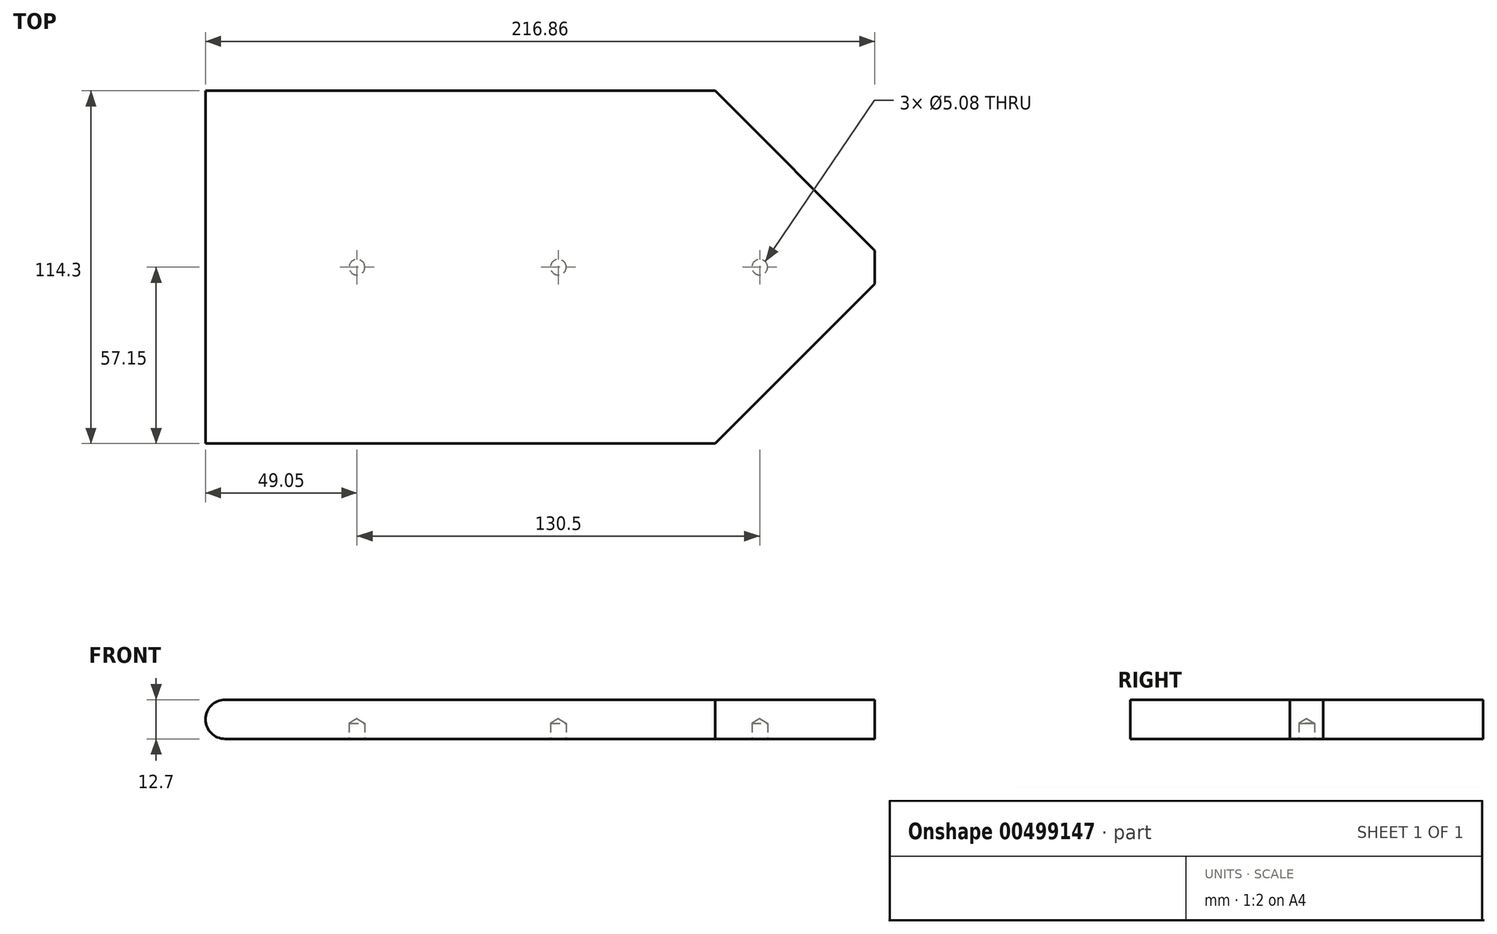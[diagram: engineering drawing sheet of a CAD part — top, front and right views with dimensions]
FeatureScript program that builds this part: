
annotation { "Feature Type Name" : "Feature", "Feature Type Description" : "" }
export const myFeature = defineFeature(function(context is Context, id is Id, definition is map)
    precondition{}
    {
        {
            var Q0;
            Q0=qCreatedBy(makeId("Top.planeOp"),FACE);
            var sketch = newSketch(context, id + "F0", { "sketchPlane" : qUnion([Q0])});
            skLineSegment(sketch, "E0.bottom", {"start": v(114.3, 57.15) * mm, "end": v(82.55, 57.15) * mm});
            skLineSegment(sketch, "E0.top", {"start": v(114.3, -57.15) * mm, "end": v(82.55, -57.15) * mm});
            skLineSegment(sketch, "E0.left", {"start": v(114.3, 57.15) * mm, "end": v(114.3, 27.94) * mm});
            skLineSegment(sketch, "E0.right", {"start": v(-114.3, 57.15) * mm, "end": v(-114.3, -57.15) * mm});
            skPoint(sketch, "E0.middle", {"position": v(0, 0) * mm});
            skLineSegment(sketch, "E1", {"start": v(0, 0) * mm, "end": v(65.25, 0) * mm});
            skLineSegment(sketch, "E2", {"start": v(65.25, 0) * mm, "end": v(0, 0) * mm, "construction": true});
            skLineSegment(sketch, "E3", {"start": v(-65.25, 0) * mm, "end": v(0, 0) * mm, "construction": true});
            skPoint(sketch, "E4", {"position": v(-65.25, 0) * mm});
            skPoint(sketch, "E5", {"position": v(65.25, 0) * mm});
            skPoint(sketch, "E6", {"position": v(126.87, 10.64) * mm});
            skLineSegment(sketch, "E7", {"start": v(82.55, -57.15) * mm, "end": v(82.55, -27.94) * mm, "construction": true});
            skLineSegment(sketch, "E8", {"start": v(82.55, -27.94) * mm, "end": v(114.3, -27.94) * mm, "construction": true});
            skLineSegment(sketch, "E9", {"start": v(82.55, 27.94) * mm, "end": v(114.3, 27.94) * mm, "construction": true});
            skLineSegment(sketch, "E10", {"start": v(82.55, 27.94) * mm, "end": v(82.55, 57.15) * mm, "construction": true});
            skLineSegment(sketch, "E11", {"start": v(114.3, -27.94) * mm, "end": v(114.3, -57.15) * mm});
            skLineSegment(sketch, "E12", {"start": v(114.3, 27.94) * mm, "end": v(114.3, -27.94) * mm});
            skLineSegment(sketch, "E13", {"start": v(82.55, -57.15) * mm, "end": v(-114.3, -57.15) * mm});
            skLineSegment(sketch, "E14", {"start": v(82.55, 57.15) * mm, "end": v(-114.3, 57.15) * mm});
            skSolve(sketch);
        }
        {
            var Q0;
            Q0=makeQuery(id+"F0.imprint","IMPRINT",FACE,{"disambiguationData":[TD([[makeQuery(id+"F0.imprint","IMPRINT",EDGE,{"derivedFrom":sQuery(id+"F0.wireOp",EDGE,"E0.right")}),1.0]])]});
            extrude(context, id + "F1", {"entities" : qUnion([Q0]), "depth" : 12.7 * mm});
        }
        {
            var Q0;
            Q0=sQuery(id+"F0.wireOp",VERTEX,"E4");
            var Q1;
            Q1=makeQuery(id+"F1.opExtrude","SWEPT_BODY",BODY,{"disambiguationData":[OSD([sQuery(id+"F0.wireOp",EDGE,"E0.bottom"),sQuery(id+"F0.wireOp",EDGE,"E0.top"),sQuery(id+"F0.wireOp",EDGE,"E0.left"),sQuery(id+"F0.wireOp",EDGE,"E0.right")])]});
            hole(context, id + "F2", {"style" : HoleStyle.SIMPLE, "endStyle" : HoleEndStyle.BLIND, "oppositeDirection" : true, "holeDiameter" : 5.08 * mm, "holeDepth" : 5.08 * mm, "isTappedThrough" : true, "tappedDepth" : 12.7 * mm, "tapClearance" : 3, "locations" : qUnion([Q0]), "scope" : qUnion([Q1])});
        }
        {
            var Q0;
            Q0=sQuery(id+"F0.wireOp",VERTEX,"E0.middle");
            var Q1;
            Q1=sQuery(id+"F0.wireOp",VERTEX,"E5");
            var Q2;
            Q2=makeQuery(id+"F1.opExtrude","SWEPT_BODY",BODY,{"disambiguationData":[OSD([sQuery(id+"F0.wireOp",EDGE,"E0.bottom"),sQuery(id+"F0.wireOp",EDGE,"E0.top"),sQuery(id+"F0.wireOp",EDGE,"E0.left"),sQuery(id+"F0.wireOp",EDGE,"E0.right")])]});
            hole(context, id + "F3", {"style" : HoleStyle.SIMPLE, "endStyle" : HoleEndStyle.BLIND, "oppositeDirection" : true, "holeDiameter" : 5.08 * mm, "holeDepth" : 5.08 * mm, "isTappedThrough" : true, "tappedDepth" : 12.7 * mm, "tapClearance" : 3, "locations" : qUnion([Q0, Q1]), "scope" : qUnion([Q2])});
        }
        {
            var Q0;
            Q0=makeQuery(id+"F1.opExtrude","SWEPT_EDGE",EDGE,{"disambiguationData":[OSD([sQuery(id+"F0.wireOp",EDGE,"E0.bottom"),sQuery(id+"F0.wireOp",EDGE,"E0.left")])]});
            var Q1;
            Q1=makeQuery(id+"F1.opExtrude","SWEPT_EDGE",EDGE,{"disambiguationData":[OSD([sQuery(id+"F0.wireOp",EDGE,"E0.top"),sQuery(id+"F0.wireOp",EDGE,"E11")])]});
            chamfer(context, id + "F4", {"entities" : qUnion([Q0, Q1]), "chamferType" : ChamferType.TWO_OFFSETS, "width1" : 63.5 * mm, "oppositeDirection" : false, "width2" : 63.5 * mm, "tangentPropagation" : true});
        }
        {
            var Q0;
            Q0=makeQuery(id+"F4.opChamfer","BLEND_EDGE",EDGE,{"blendedFrom":[makeQuery(id+"F1.opExtrude","SWEPT_EDGE",EDGE,{"disambiguationData":[OSD([sQuery(id+"F0.wireOp",EDGE,"E0.bottom"),sQuery(id+"F0.wireOp",EDGE,"E0.left")])]}),makeQuery(id+"F1.opExtrude","SWEPT_EDGE",EDGE,{"disambiguationData":[OSD([sQuery(id+"F0.wireOp",EDGE,"E0.top"),sQuery(id+"F0.wireOp",EDGE,"E11")])]})],"blendedInto":[]});
            chamfer(context, id + "F5", {"entities" : qUnion([Q0]), "width" : 7.62 * mm, "tangentPropagation" : true});
        }
        {
            var Q0;
            Q0=makeQuery(id+"F1.opExtrude","CAP_EDGE",EDGE,{"disambiguationData":[OSD([sQuery(id+"F0.wireOp",EDGE,"E0.right")])],"isStart":true});
            var Q1;
            Q1=makeQuery(id+"F1.opExtrude","CAP_EDGE",EDGE,{"disambiguationData":[OSD([sQuery(id+"F0.wireOp",EDGE,"E0.right")])],"isStart":false});
            fillet(context, id + "F6", {"entities" : qUnion([Q0, Q1]), "radius" : 6.35 * mm, "tangentPropagation" : true, "allowEdgeOverflow" : false});
        }
    });
